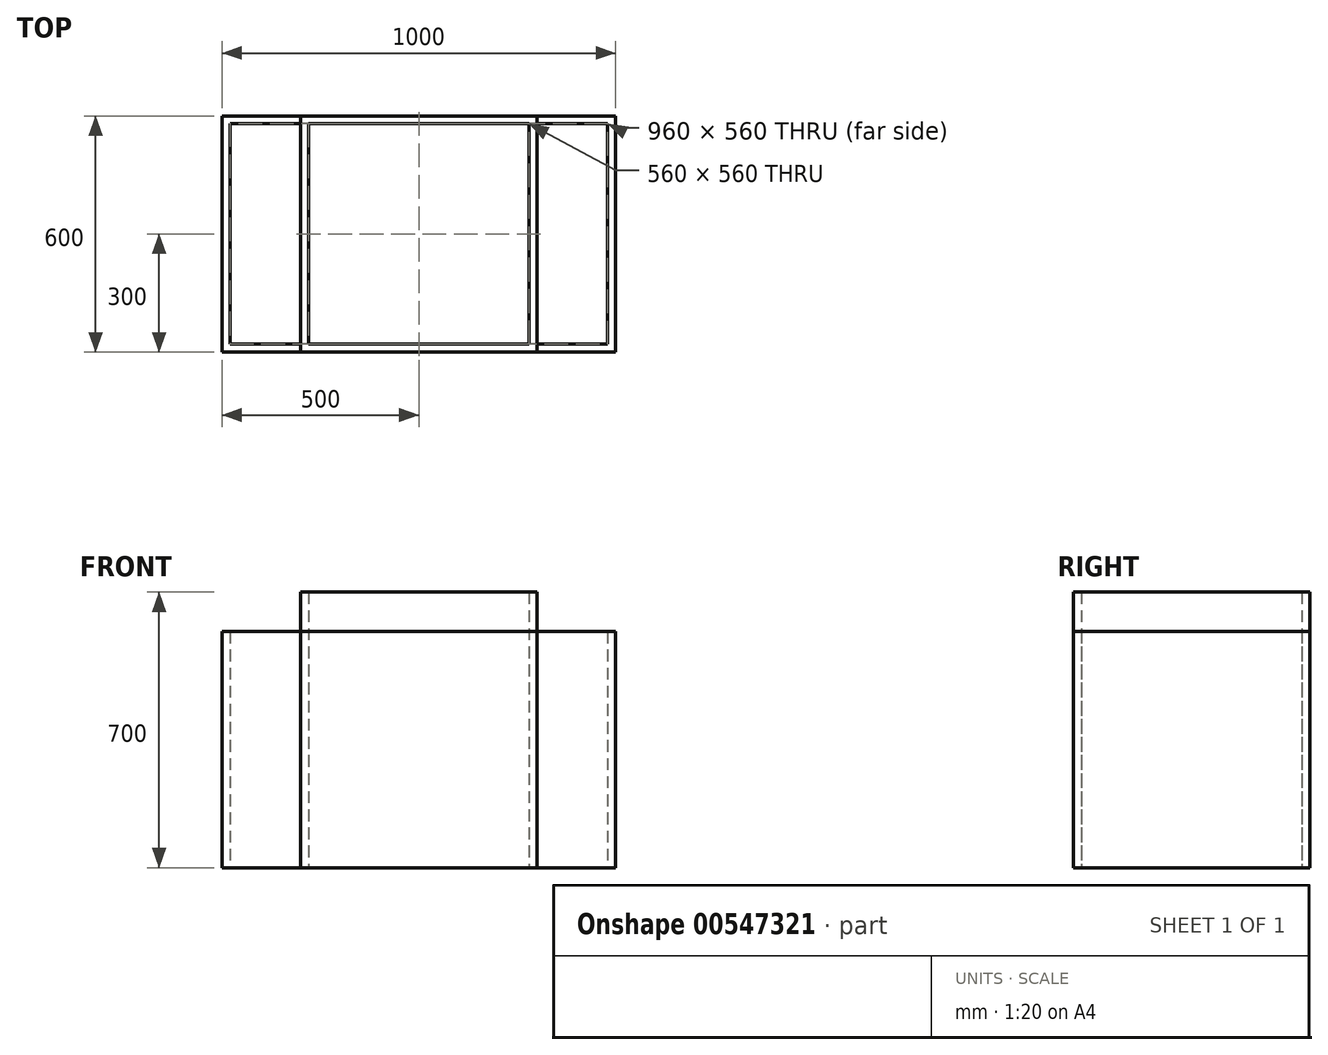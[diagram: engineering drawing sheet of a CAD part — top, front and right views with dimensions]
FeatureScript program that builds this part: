
annotation { "Feature Type Name" : "Feature", "Feature Type Description" : "" }
export const myFeature = defineFeature(function(context is Context, id is Id, definition is map)
    precondition{}
    {
        {
            var Q0;
            Q0=qCreatedBy(makeId("Top.planeOp"),FACE);
            var sketch = newSketch(context, id + "F0", { "sketchPlane" : qUnion([Q0])});
            skLineSegment(sketch, "E0.bottom", {"start": v(300, -300) * mm, "end": v(-300, -300) * mm});
            skLineSegment(sketch, "E0.top", {"start": v(300, 300) * mm, "end": v(-300, 300) * mm});
            skLineSegment(sketch, "E0.left", {"start": v(300, -300) * mm, "end": v(300, 300) * mm});
            skLineSegment(sketch, "E0.right", {"start": v(-300, -300) * mm, "end": v(-300, 300) * mm});
            skPoint(sketch, "E0.middle", {"position": v(0, 0) * mm});
            skLineSegment(sketch, "E1.bottom", {"start": v(280, 280) * mm, "end": v(-280, 280) * mm});
            skLineSegment(sketch, "E1.top", {"start": v(280, -280) * mm, "end": v(-280, -280) * mm});
            skLineSegment(sketch, "E1.left", {"start": v(280, 280) * mm, "end": v(280, -280) * mm});
            skLineSegment(sketch, "E1.right", {"start": v(-280, 280) * mm, "end": v(-280, -280) * mm});
            skSolve(sketch);
        }
        {
            var Q0;
            Q0=makeQuery(id+"F0.imprint","IMPRINT",FACE,{"disambiguationData":[TD([[makeQuery(id+"F0.imprint","IMPRINT",EDGE,{"derivedFrom":sQuery(id+"F0.wireOp",EDGE,"E0.bottom")}),-1.0]])]});
            extrude(context, id + "F1", {"entities" : qUnion([Q0]), "depth" : 700 * mm, "offsetDistance" : 25 * mm});
        }
        {
            var Q0;
            Q0=qCreatedBy(makeId("Top.planeOp"),FACE);
            var sketch = newSketch(context, id + "F2", { "sketchPlane" : qUnion([Q0])});
            skLineSegment(sketch, "E2.bottom", {"start": v(500, -300) * mm, "end": v(-500, -300) * mm});
            skLineSegment(sketch, "E2.top", {"start": v(500, 300) * mm, "end": v(-500, 300) * mm});
            skLineSegment(sketch, "E2.left", {"start": v(500, -300) * mm, "end": v(500, 300) * mm});
            skLineSegment(sketch, "E2.right", {"start": v(-500, -300) * mm, "end": v(-500, 300) * mm});
            skPoint(sketch, "E2.middle", {"position": v(0, 0) * mm});
            skLineSegment(sketch, "E3.bottom", {"start": v(480, -280) * mm, "end": v(-480, -280) * mm});
            skLineSegment(sketch, "E3.top", {"start": v(480, 280) * mm, "end": v(-480, 280) * mm});
            skLineSegment(sketch, "E3.left", {"start": v(480, -280) * mm, "end": v(480, 280) * mm});
            skLineSegment(sketch, "E3.right", {"start": v(-480, -280) * mm, "end": v(-480, 280) * mm});
            skSolve(sketch);
        }
        {
            var Q0;
            Q0=makeQuery(id+"F2.imprint","IMPRINT",FACE,{"disambiguationData":[TD([[makeQuery(id+"F2.imprint","IMPRINT",EDGE,{"derivedFrom":sQuery(id+"F2.wireOp",EDGE,"E2.bottom")}),-1.0]])]});
            extrude(context, id + "F3", {"entities" : qUnion([Q0]), "depth" : 600 * mm, "offsetDistance" : 25 * mm});
        }
    });
